# Revit family: Navicula Small
name_source: partatom
category: Lighting Fixtures
revit_build: Autodesk Revit 2017 (Build: 20160225_1515(x64)
units: mm (PartAtom-declared; Revit-internal decimal feet)

## family parameters
Always vertical = Yes
Cut with Voids When Loaded = No
Host = Ceiling
Light Source = Yes
OmniClass Number = 23.80.70.11
OmniClass Title = Luminaries for Internal Lighting
Part Type = Normal
Room Calculation Point = No
Round Connector Dimension = Use Diameter
Shared = No

## types (2) — shared parameters
Apparent Load = 0 VA
Canopy length = 380 mm
Color Filter = 16777215
Cordset Finish = Plastic, Opaque White
Description = Pendant in bamboo plywood with LED light source. Can be made in a large range of colours
Dimming Lamp Color Temperature Shift = <None>
Emit from Line Length = 800 mm  [stored 2.62467 ft]
Lamp = Linear LED
Light Source Symbol Size = 100 mm  [stored 0.328084 ft]
Manufacturer = David Trubridge
Suspension Cable Finish = Stainless Steel, Brushed
URL = https://www.davidtrubridge.com

## per-type parameters (varying)
| type | Canopy location | Connection elevation | Lamp Wattage | Model | Type Comments | Wattage Comments |
| Surface mounted driver (EU) | 40 mm  [stored 0.131234 ft] | 40 mm  [stored 0.131234 ft] | 11 W | Navicula Small | Confirm with supplier for suitable installation | 230-240V (EU) |
| Remote Driver (EU/US) | 200 mm | 0 mm  [stored 0 ft] | 0 W | Navicula Medium | Remote driver location shown as example only | 110V(US) / 230-240V(EU). |

note: [stored X ft] marks values corroborated as IEEE doubles in the binary element streams (Revit-internal decimal feet)

## geometry (parser evidence)
native form markers: Sweep x3
no freeform markers — native parametric forms only
